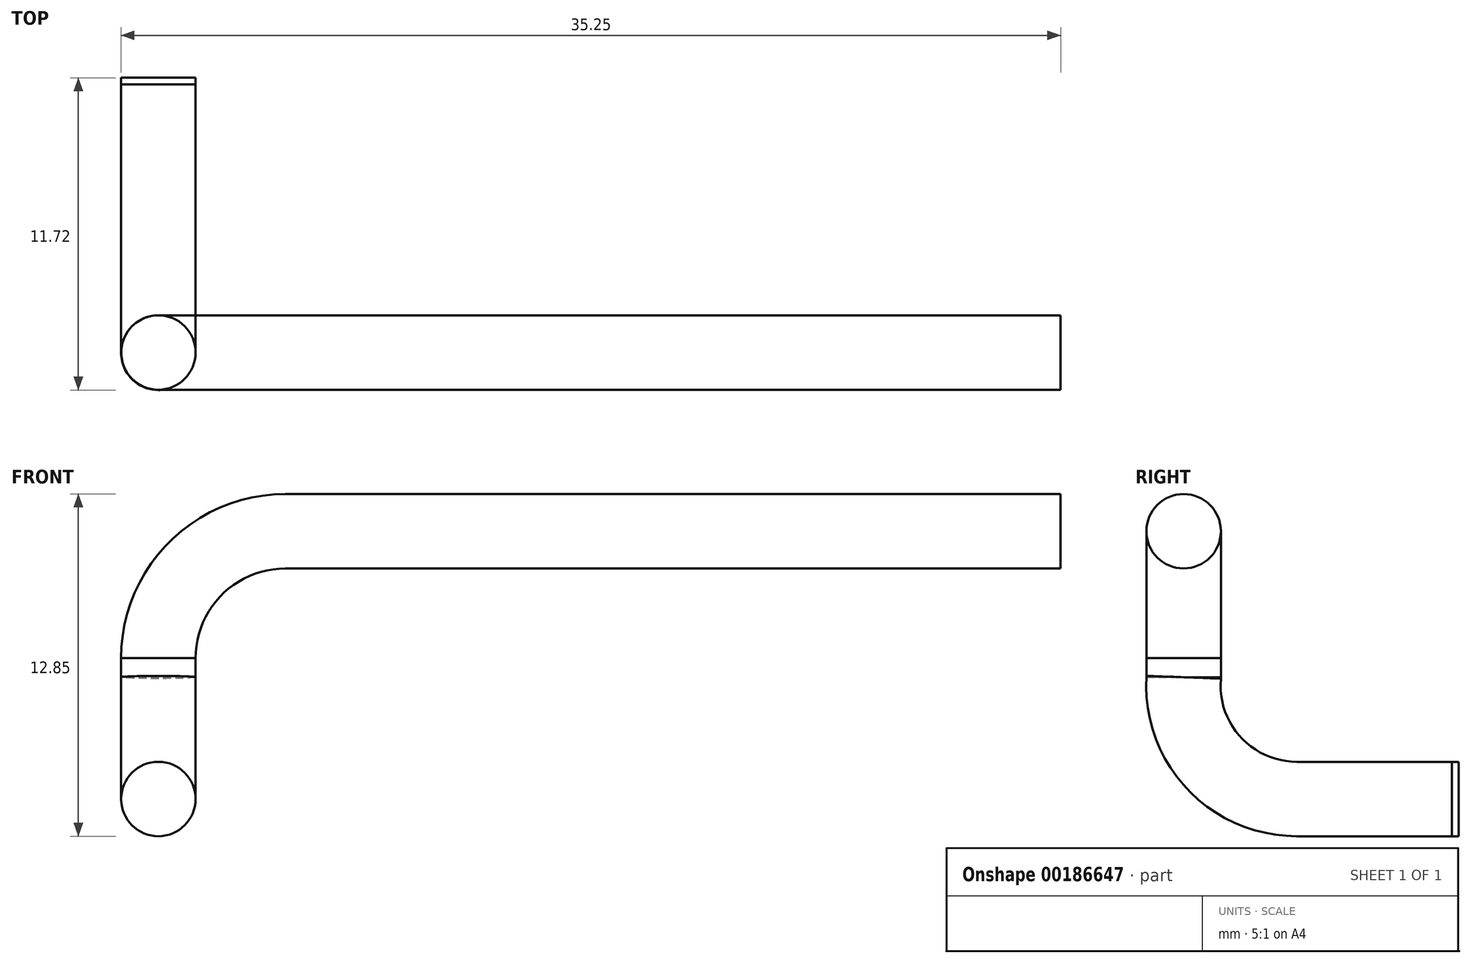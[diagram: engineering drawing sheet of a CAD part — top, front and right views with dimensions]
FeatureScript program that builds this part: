
annotation { "Feature Type Name" : "Feature", "Feature Type Description" : "" }
export const myFeature = defineFeature(function(context is Context, id is Id, definition is map)
    precondition{}
    {
        {
            var Q0;
            Q0=qCreatedBy(makeId("Front.planeOp"),FACE);
            var sketch = newSketch(context, id + "F0", { "sketchPlane" : qUnion([Q0])});
            skLineSegment(sketch, "E0", {"start": v(33.34, 5.48) * mm, "end": v(4.76, 5.48) * mm});
            skArc(sketch, "E1", {"start": v(4.76, 5.48) * mm, "mid": v(1.4, 4.09) * mm, "end": v(0, 0.72) * mm});
            skLineSegment(sketch, "E2", {"start": v(0, 0.72) * mm, "end": v(0, 0) * mm});
            skSolve(sketch);
        }
        {
            var Q0;
            Q0=qCreatedBy(makeId("Right.planeOp"),FACE);
            cPlane(context, id + "F1", {"entities" : qUnion([Q0]), "cplaneType" : CPlaneType.OFFSET, "offset" : 33.34 * mm, "width" : 152.4 * mm, "height" : 152.4 * mm});
        }
        {
            var Q0;
            Q0=qCreatedBy(id+"F1.planeOp",FACE);
            var sketch = newSketch(context, id + "F2", { "sketchPlane" : qUnion([Q0])});
            skCircle(sketch, "E3", {"center": v(0, 5.48) * mm, "radius": 1.4 * mm});
            skSolve(sketch);
        }
        {
            var Q0;
            Q0=makeQuery(id+"F2.imprint","IMPRINT",FACE,{"disambiguationData":[TD([[makeQuery(id+"F2.imprint","IMPRINT",EDGE,{"derivedFrom":sQuery(id+"F2.wireOp",EDGE,"E3")}),1.0]])]});
            var Q1;
            Q1=sQuery(id+"F0.wireOp",EDGE,"E0");
            var Q2;
            Q2=sQuery(id+"F0.wireOp",EDGE,"E1");
            var Q3;
            Q3=sQuery(id+"F0.wireOp",EDGE,"E2");
            sweep(context, id + "F3", {"profiles" : qUnion([Q0]), "path" : qUnion([Q1, Q2, Q3])});
        }
        {
            var Q0;
            Q0=qCreatedBy(makeId("Front.planeOp"),FACE);
            cPlane(context, id + "F4", {"entities" : qUnion([Q0]), "cplaneType" : CPlaneType.OFFSET, "offset" : 10.06 * mm, "oppositeDirection" : true, "width" : 152.4 * mm, "height" : 152.4 * mm});
        }
        {
            var Q0;
            Q0=qCreatedBy(makeId("Right.planeOp"),FACE);
            var sketch = newSketch(context, id + "F5", { "sketchPlane" : qUnion([Q0])});
            skLineSegment(sketch, "E4", {"start": v(0, 0) * mm, "end": v(0, -4.57) * mm, "construction": true});
            skLineSegment(sketch, "E5", {"start": v(0, 5.48) * mm, "end": v(10.06, 5.48) * mm, "construction": true});
            skPoint(sketch, "E5.startSnap0", {"position": v(0, -2.29) * mm});
            skLineSegment(sketch, "E6", {"start": v(10.06, -4.57) * mm, "end": v(4.24, -4.57) * mm});
            skArc(sketch, "E7", {"start": v(4.24, -4.57) * mm, "mid": v(1.13, -3.21) * mm, "end": v(0, 0) * mm});
            skLineSegment(sketch, "E8", {"start": v(4.24, -4.57) * mm, "end": v(0, -4.57) * mm, "construction": true});
            skLineSegment(sketch, "E9", {"start": v(0, 0) * mm, "end": v(0, 0.25) * mm});
            skLineSegment(sketch, "E10", {"start": v(0, 0) * mm, "end": v(4.24, 0) * mm, "construction": true});
            skLineSegment(sketch, "E11", {"start": v(4.24, 0) * mm, "end": v(4.24, -0.32) * mm, "construction": true});
            skLineSegment(sketch, "E12", {"start": v(4.24, 0) * mm, "end": v(10.06, 0) * mm, "construction": true});
            skLineSegment(sketch, "E13", {"start": v(10.06, -4.57) * mm, "end": v(10.06, 0) * mm, "construction": true});
            skLineSegment(sketch, "E14", {"start": v(10.06, 0) * mm, "end": v(10.06, 5.48) * mm, "construction": true});
            skSolve(sketch);
        }
        {
            var Q0;
            Q0=qCreatedBy(id+"F4.planeOp",FACE);
            var sketch = newSketch(context, id + "F6", { "sketchPlane" : qUnion([Q0])});
            skCircle(sketch, "E15", {"center": v(0, -4.57) * mm, "radius": 1.4 * mm});
            skSolve(sketch);
        }
        {
            var Q0;
            Q0=makeQuery(id+"F6.imprint","IMPRINT",FACE,{"disambiguationData":[TD([[makeQuery(id+"F6.imprint","IMPRINT",EDGE,{"derivedFrom":sQuery(id+"F6.wireOp",EDGE,"E15")}),1.0]])]});
            var Q1;
            Q1=sQuery(id+"F6.wireOp",EDGE,"E15");
            var Q2;
            Q2=sQuery(id+"F5.wireOp",EDGE,"E6");
            var Q3;
            Q3=sQuery(id+"F5.wireOp",EDGE,"E7");
            var Q4;
            Q4=sQuery(id+"F0.wireOp",EDGE,"E2");
            sweep(context, id + "F7", {"profiles" : qUnion([Q0]), "surfaceProfiles" : qUnion([Q1]), "path" : qUnion([Q2, Q3, Q4])});
        }
        {
            var Q0;
            Q0=makeQuery(id+"F6.imprint","IMPRINT",FACE,{"disambiguationData":[TD([[makeQuery(id+"F6.imprint","IMPRINT",EDGE,{"derivedFrom":sQuery(id+"F6.wireOp",EDGE,"E15")}),1.0]])]});
            var Q1;
            Q1=sQuery(id+"F6.wireOp",EDGE,"E15");
            extrude(context, id + "F8", {"entities" : qUnion([Q0]), "surfaceEntities" : qUnion([Q1]), "oppositeDirection" : true, "depth" : 0.25 * mm});
        }
        {
            var Q0;
            Q0=makeQuery(id+"F2.imprint","IMPRINT",FACE,{"disambiguationData":[TD([[makeQuery(id+"F2.imprint","IMPRINT",EDGE,{"derivedFrom":sQuery(id+"F2.wireOp",EDGE,"E3")}),1.0]])]});
            extrude(context, id + "F9", {"entities" : qUnion([Q0]), "operationType" : NewBodyOperationType.ADD, "depth" : 0.5 * mm});
        }
    });
